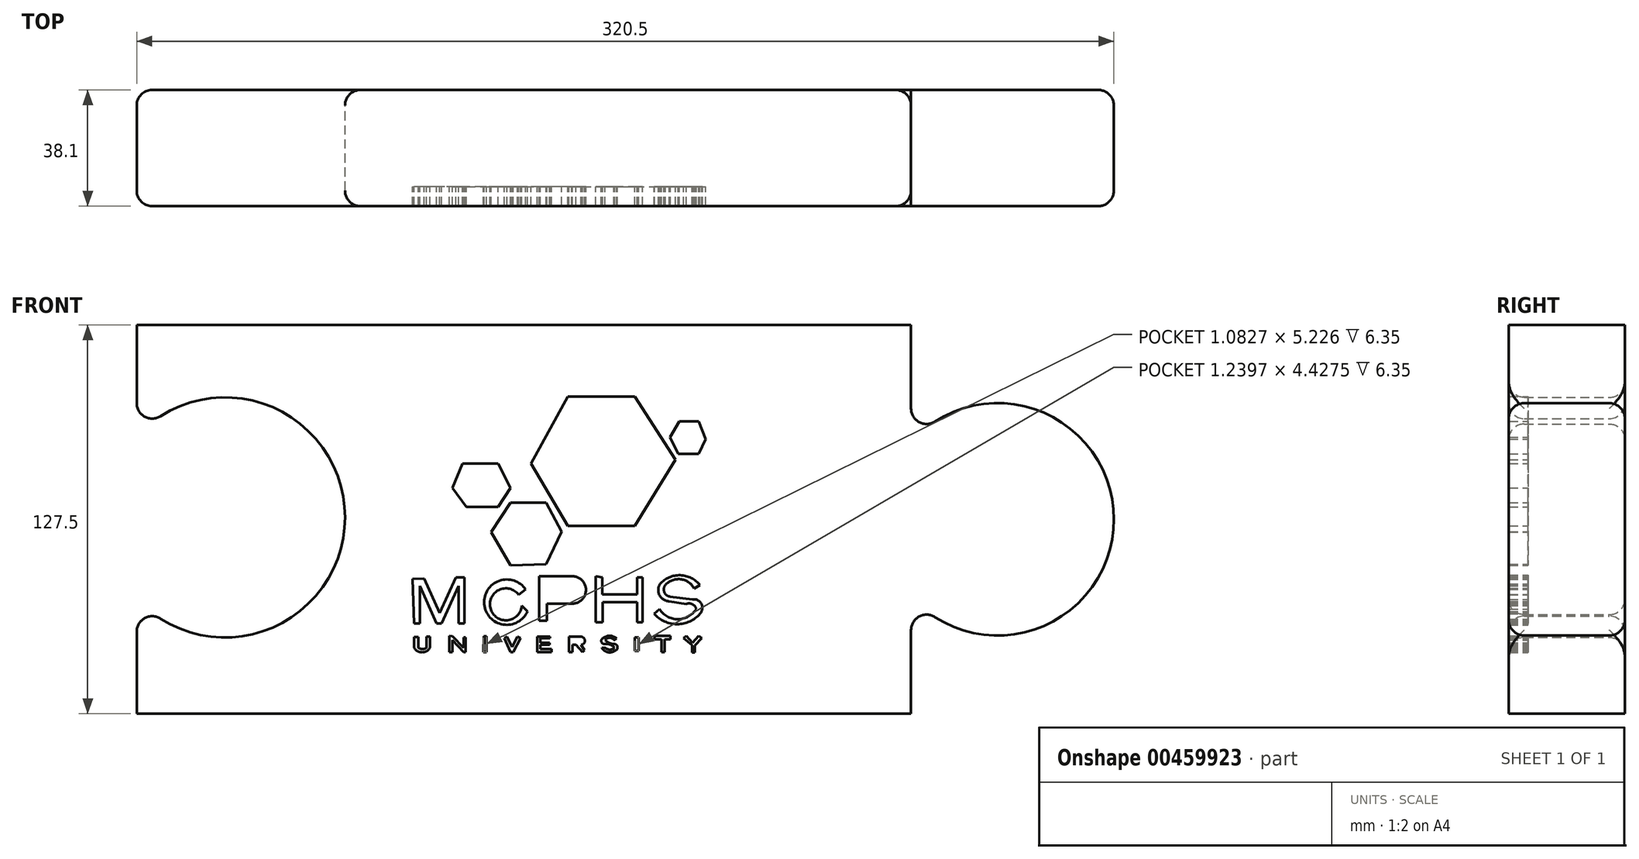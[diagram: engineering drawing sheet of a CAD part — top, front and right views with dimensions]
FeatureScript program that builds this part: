
annotation { "Feature Type Name" : "Feature", "Feature Type Description" : "" }
export const myFeature = defineFeature(function(context is Context, id is Id, definition is map)
    precondition{}
    {
        {
            var Q0;
            Q0=qCreatedBy(makeId("Front.planeOp"),FACE);
            var sketch = newSketch(context, id + "F0", { "sketchPlane" : qUnion([Q0])});
            skLineSegment(sketch, "E0", {"start": v(-152.36, 71.31) * mm, "end": v(101.64, 71.31) * mm, "construction": true});
            skLineSegment(sketch, "E1", {"start": v(-152.36, -56.2) * mm, "end": v(101.64, -56.2) * mm, "construction": true});
            skArc(sketch, "E2", {"start": v(101.64, -17.84) * mm, "mid": v(168.14, 7.56) * mm, "end": v(101.64, 32.96) * mm, "construction": true});
            skLineSegment(sketch, "E3", {"start": v(-152.36, -56.2) * mm, "end": v(-152.36, -18.47) * mm});
            skLineSegment(sketch, "E4", {"start": v(-152.36, -56.2) * mm, "end": v(101.64, -56.2) * mm});
            skLineSegment(sketch, "E5", {"start": v(101.64, -17.84) * mm, "end": v(101.64, -56.2) * mm});
            skLineSegment(sketch, "E6", {"start": v(101.64, 32.96) * mm, "end": v(101.64, 71.31) * mm});
            skLineSegment(sketch, "E7", {"start": v(-152.36, 71.31) * mm, "end": v(101.64, 71.31) * mm});
            skLineSegment(sketch, "E8", {"start": v(-152.36, 71.31) * mm, "end": v(-152.36, 34.87) * mm});
            skArc(sketch, "E9", {"start": v(-152.36, -18.47) * mm, "mid": v(-84.03, 8.2) * mm, "end": v(-152.36, 34.87) * mm});
            skArc(sketch, "E10", {"start": v(101.64, -17.84) * mm, "mid": v(168.14, 7.56) * mm, "end": v(101.64, 32.96) * mm});
            skLineSegment(sketch, "E11", {"start": v(-23.03, 25.82) * mm, "end": v(-10.96, 5.44) * mm});
            skLineSegment(sketch, "E12", {"start": v(-10.96, 5.44) * mm, "end": v(11.08, 5.44) * mm});
            skLineSegment(sketch, "E13", {"start": v(11.08, 5.44) * mm, "end": v(24.4, 27.07) * mm});
            skLineSegment(sketch, "E14", {"start": v(24.4, 27.07) * mm, "end": v(11.08, 47.87) * mm});
            skLineSegment(sketch, "E15", {"start": v(11.08, 47.87) * mm, "end": v(-10.96, 47.87) * mm});
            skLineSegment(sketch, "E16", {"start": v(-10.96, 47.87) * mm, "end": v(-23.03, 25.82) * mm});
            skLineSegment(sketch, "E17", {"start": v(-45.49, 25.82) * mm, "end": v(-33.84, 25.82) * mm});
            skLineSegment(sketch, "E18", {"start": v(-33.84, 25.82) * mm, "end": v(-29.68, 17.92) * mm});
            skLineSegment(sketch, "E19", {"start": v(-29.68, 17.92) * mm, "end": v(-33.84, 11.68) * mm});
            skLineSegment(sketch, "E20", {"start": v(-33.84, 11.68) * mm, "end": v(-44.24, 11.68) * mm});
            skLineSegment(sketch, "E21", {"start": v(-44.24, 11.68) * mm, "end": v(-48.82, 17.92) * mm});
            skLineSegment(sketch, "E22", {"start": v(-48.82, 17.92) * mm, "end": v(-45.49, 25.82) * mm});
            skLineSegment(sketch, "E23", {"start": v(-29.68, -7.55) * mm, "end": v(-36.12, 3.33) * mm});
            skLineSegment(sketch, "E24", {"start": v(-36.12, 3.33) * mm, "end": v(-29.68, 13) * mm});
            skLineSegment(sketch, "E25", {"start": v(-29.68, 13) * mm, "end": v(-18, 13) * mm});
            skLineSegment(sketch, "E26", {"start": v(-18, 13) * mm, "end": v(-12.99, 3.54) * mm});
            skLineSegment(sketch, "E27", {"start": v(-12.99, 3.54) * mm, "end": v(-18, -7.13) * mm});
            skLineSegment(sketch, "E28", {"start": v(-18, -7.13) * mm, "end": v(-29.68, -7.55) * mm});
            skLineSegment(sketch, "E29", {"start": v(22.57, 34.5) * mm, "end": v(25.3, 29.06) * mm});
            skLineSegment(sketch, "E30", {"start": v(25.3, 29.06) * mm, "end": v(31.99, 29.06) * mm});
            skLineSegment(sketch, "E31", {"start": v(31.99, 29.06) * mm, "end": v(34.29, 33.87) * mm});
            skLineSegment(sketch, "E32", {"start": v(34.29, 33.87) * mm, "end": v(31.99, 39.76) * mm});
            skLineSegment(sketch, "E33", {"start": v(31.99, 39.76) * mm, "end": v(25.66, 39.76) * mm});
            skLineSegment(sketch, "E34", {"start": v(25.66, 39.76) * mm, "end": v(22.57, 34.5) * mm});
            skLineSegment(sketch, "E35", {"start": v(-61.37, -26.57) * mm, "end": v(-59.5, -26.57) * mm});
            skLineSegment(sketch, "E36", {"start": v(-59.5, -26.57) * mm, "end": v(-59.5, -14.23) * mm});
            skLineSegment(sketch, "E37", {"start": v(-59.5, -14.23) * mm, "end": v(-54.05, -26.57) * mm});
            skLineSegment(sketch, "E38", {"start": v(-54.05, -26.57) * mm, "end": v(-52.38, -26.57) * mm});
            skLineSegment(sketch, "E39", {"start": v(-52.38, -26.57) * mm, "end": v(-46.73, -14.23) * mm});
            skLineSegment(sketch, "E40", {"start": v(-46.73, -14.23) * mm, "end": v(-46.73, -26.57) * mm});
            skLineSegment(sketch, "E41", {"start": v(-46.73, -26.57) * mm, "end": v(-44.85, -26.57) * mm});
            skLineSegment(sketch, "E42", {"start": v(-44.85, -26.57) * mm, "end": v(-44.85, -11.5) * mm});
            skLineSegment(sketch, "E43", {"start": v(-61.37, -26.57) * mm, "end": v(-61.9, -11.94) * mm});
            skLineSegment(sketch, "E44", {"start": v(-61.9, -11.94) * mm, "end": v(-58.03, -11.8) * mm});
            skLineSegment(sketch, "E45", {"start": v(-58.03, -11.8) * mm, "end": v(-53, -23.22) * mm});
            skLineSegment(sketch, "E46", {"start": v(-53, -23.22) * mm, "end": v(-47.64, -11.5) * mm});
            skLineSegment(sketch, "E47", {"start": v(-47.64, -11.5) * mm, "end": v(-44.85, -11.5) * mm});
            skArc(sketch, "E48", {"start": v(-24.77, -15.48) * mm, "mid": v(-38.37, -20.26) * mm, "end": v(-24.14, -22.6) * mm});
            skLineSegment(sketch, "E49", {"start": v(-24.14, -22.6) * mm, "end": v(-26.02, -20.7) * mm});
            skLineSegment(sketch, "E50", {"start": v(-24.77, -15.48) * mm, "end": v(-27.07, -17.15) * mm});
            skArc(sketch, "E51", {"start": v(-27.07, -17.15) * mm, "mid": v(-36.27, -21.8) * mm, "end": v(-26.02, -20.7) * mm});
            skLineSegment(sketch, "E52", {"start": v(-17.86, -25.73) * mm, "end": v(-20.37, -25.73) * mm});
            skLineSegment(sketch, "E53", {"start": v(-20.37, -25.73) * mm, "end": v(-20.37, -11.09) * mm});
            skLineSegment(sketch, "E54", {"start": v(-20.37, -11.09) * mm, "end": v(-9.5, -11.09) * mm});
            skLineSegment(sketch, "E55", {"start": v(-17.86, -25.73) * mm, "end": v(-17.86, -20.08) * mm});
            skLineSegment(sketch, "E56", {"start": v(-17.86, -20.08) * mm, "end": v(-9.7, -20.08) * mm});
            skLineSegment(sketch, "E57", {"start": v(-17.86, -17.78) * mm, "end": v(-18.03, -13.17) * mm});
            skLineSegment(sketch, "E58", {"start": v(-18.03, -13.17) * mm, "end": v(-10.33, -13.17) * mm});
            skLineSegment(sketch, "E59", {"start": v(-17.86, -17.78) * mm, "end": v(-9.7, -17.49) * mm});
            skArc(sketch, "E60", {"start": v(-9.7, -17.49) * mm, "mid": v(-7.61, -14.98) * mm, "end": v(-10.33, -13.17) * mm});
            skArc(sketch, "E61", {"start": v(-9.7, -20.08) * mm, "mid": v(-5, -15.69) * mm, "end": v(-9.5, -11.09) * mm});
            skLineSegment(sketch, "E62", {"start": v(0.34, -17.1) * mm, "end": v(0.34, -11.46) * mm});
            skLineSegment(sketch, "E63", {"start": v(0.34, -17.1) * mm, "end": v(11.84, -17.1) * mm});
            skLineSegment(sketch, "E64", {"start": v(11.84, -17.57) * mm, "end": v(11.84, -11.46) * mm});
            skLineSegment(sketch, "E65", {"start": v(11.84, -11.46) * mm, "end": v(13.52, -11.46) * mm});
            skLineSegment(sketch, "E66", {"start": v(13.52, -11.46) * mm, "end": v(13.52, -26.15) * mm});
            skLineSegment(sketch, "E67", {"start": v(13.52, -26.15) * mm, "end": v(11.84, -26.15) * mm});
            skLineSegment(sketch, "E68", {"start": v(11.84, -26.15) * mm, "end": v(11.84, -19.57) * mm});
            skLineSegment(sketch, "E69", {"start": v(11.84, -19.57) * mm, "end": v(0.44, -19.57) * mm});
            skLineSegment(sketch, "E70", {"start": v(0.44, -19.57) * mm, "end": v(0.44, -26.15) * mm});
            skLineSegment(sketch, "E71", {"start": v(0.44, -26.15) * mm, "end": v(-1.84, -26.15) * mm});
            skLineSegment(sketch, "E72", {"start": v(-1.84, -26.15) * mm, "end": v(-1.84, -11.11) * mm});
            skLineSegment(sketch, "E73", {"start": v(-1.84, -11.11) * mm, "end": v(0.34, -11.46) * mm});
            skArc(sketch, "E74", {"start": v(32.42, -14.05) * mm, "mid": v(25.94, -10.78) * mm, "end": v(19.29, -13.67) * mm});
            skLineSegment(sketch, "E75", {"start": v(32.42, -14.05) * mm, "end": v(30.44, -15.1) * mm});
            skLineSegment(sketch, "E76", {"start": v(19.1, -21.86) * mm, "end": v(17.38, -23.38) * mm});
            skPoint(sketch, "E77.endSnap0", {"position": v(13.52, -18.8) * mm});
            skArc(sketch, "E78", {"start": v(19.1, -21.86) * mm, "mid": v(25.14, -25.2) * mm, "end": v(31.18, -21.86) * mm});
            skArc(sketch, "E79", {"start": v(31.18, -21.86) * mm, "mid": v(29.92, -20.3) * mm, "end": v(27.92, -20.18) * mm});
            skArc(sketch, "E80", {"start": v(19.29, -13.67) * mm, "mid": v(19.16, -17.38) * mm, "end": v(22.33, -19.32) * mm});
            skLineSegment(sketch, "E81", {"start": v(22.33, -19.32) * mm, "end": v(27.92, -20.18) * mm});
            skArc(sketch, "E82", {"start": v(30.44, -15.1) * mm, "mid": v(26, -12.08) * mm, "end": v(21.01, -14.05) * mm});
            skArc(sketch, "E83", {"start": v(21.01, -14.05) * mm, "mid": v(20.72, -16.36) * mm, "end": v(22.57, -17.78) * mm});
            skArc(sketch, "E84", {"start": v(17.38, -23.38) * mm, "mid": v(24.9, -26.81) * mm, "end": v(32.42, -23.38) * mm});
            skArc(sketch, "E85", {"start": v(32.42, -23.38) * mm, "mid": v(32.86, -20.13) * mm, "end": v(29.92, -18.7) * mm});
            skPoint(sketch, "E85.endSnap0", {"position": v(29.92, -20.3) * mm});
            skLineSegment(sketch, "E86", {"start": v(22.57, -17.78) * mm, "end": v(29.92, -18.7) * mm});
            skLineSegment(sketch, "E87", {"start": v(-61.32, -31.06) * mm, "end": v(-61.32, -34.58) * mm});
            skLineSegment(sketch, "E88", {"start": v(-56.2, -30.93) * mm, "end": v(-56.2, -34.58) * mm});
            skLineSegment(sketch, "E89", {"start": v(-56.2, -30.93) * mm, "end": v(-57.3, -30.93) * mm});
            skLineSegment(sketch, "E90", {"start": v(-57.3, -30.93) * mm, "end": v(-57.3, -34.58) * mm});
            skLineSegment(sketch, "E91", {"start": v(-61.32, -31.06) * mm, "end": v(-59.93, -31.06) * mm});
            skLineSegment(sketch, "E92", {"start": v(-59.93, -31.06) * mm, "end": v(-59.93, -34.58) * mm});
            skArc(sketch, "E93", {"start": v(-61.32, -34.58) * mm, "mid": v(-58.76, -36.06) * mm, "end": v(-56.2, -34.58) * mm});
            skArc(sketch, "E94", {"start": v(-59.93, -34.58) * mm, "mid": v(-58.62, -34.98) * mm, "end": v(-57.3, -34.58) * mm});
            skLineSegment(sketch, "E95", {"start": v(-49.86, -35.96) * mm, "end": v(-48.85, -35.96) * mm});
            skLineSegment(sketch, "E96", {"start": v(-48.85, -35.96) * mm, "end": v(-48.85, -32.07) * mm});
            skLineSegment(sketch, "E97", {"start": v(-48.85, -32.07) * mm, "end": v(-45.16, -35.96) * mm});
            skLineSegment(sketch, "E98", {"start": v(-45.16, -35.96) * mm, "end": v(-44.48, -35.96) * mm});
            skLineSegment(sketch, "E99", {"start": v(-44.48, -35.96) * mm, "end": v(-44.48, -31.18) * mm});
            skLineSegment(sketch, "E100", {"start": v(-44.48, -31.18) * mm, "end": v(-45.16, -31.18) * mm});
            skLineSegment(sketch, "E101", {"start": v(-45.16, -31.18) * mm, "end": v(-45.16, -34.62) * mm});
            skLineSegment(sketch, "E102", {"start": v(-45.16, -34.62) * mm, "end": v(-48.85, -30.73) * mm});
            skLineSegment(sketch, "E103", {"start": v(-49.86, -35.96) * mm, "end": v(-49.86, -30.61) * mm});
            skLineSegment(sketch, "E104", {"start": v(-49.86, -30.61) * mm, "end": v(-48.85, -30.73) * mm});
            skLineSegment(sketch, "E105", {"start": v(-38.66, -35.96) * mm, "end": v(-37.58, -35.96) * mm});
            skLineSegment(sketch, "E106", {"start": v(-37.58, -35.96) * mm, "end": v(-37.58, -30.73) * mm});
            skLineSegment(sketch, "E107", {"start": v(-37.58, -30.73) * mm, "end": v(-38.57, -30.73) * mm});
            skLineSegment(sketch, "E108", {"start": v(-38.57, -30.73) * mm, "end": v(-38.66, -35.96) * mm});
            skLineSegment(sketch, "E109", {"start": v(-31.77, -31.4) * mm, "end": v(-29.76, -35.96) * mm});
            skLineSegment(sketch, "E110", {"start": v(-29.76, -35.96) * mm, "end": v(-28.83, -35.96) * mm});
            skLineSegment(sketch, "E111", {"start": v(-28.83, -35.96) * mm, "end": v(-26.46, -31.42) * mm});
            skLineSegment(sketch, "E112", {"start": v(-26.46, -31.42) * mm, "end": v(-27.4, -30.94) * mm});
            skLineSegment(sketch, "E113", {"start": v(-27.4, -30.94) * mm, "end": v(-29.2, -34.38) * mm});
            skLineSegment(sketch, "E114", {"start": v(-29.2, -34.38) * mm, "end": v(-30.9, -30.94) * mm});
            skLineSegment(sketch, "E115", {"start": v(-30.9, -30.94) * mm, "end": v(-31.77, -31.4) * mm});
            skLineSegment(sketch, "E116", {"start": v(-20.96, -30.94) * mm, "end": v(-20.96, -35.96) * mm});
            skLineSegment(sketch, "E117", {"start": v(-20.96, -35.96) * mm, "end": v(-16.22, -35.96) * mm});
            skLineSegment(sketch, "E118", {"start": v(-16.22, -35.96) * mm, "end": v(-16.22, -35.01) * mm});
            skLineSegment(sketch, "E119", {"start": v(-16.22, -35.01) * mm, "end": v(-19.92, -35.01) * mm});
            skLineSegment(sketch, "E120", {"start": v(-19.92, -35.01) * mm, "end": v(-19.92, -33.61) * mm});
            skLineSegment(sketch, "E121", {"start": v(-19.92, -33.61) * mm, "end": v(-16.97, -33.61) * mm});
            skLineSegment(sketch, "E122", {"start": v(-16.97, -33.61) * mm, "end": v(-16.97, -32.9) * mm});
            skLineSegment(sketch, "E123", {"start": v(-16.97, -32.9) * mm, "end": v(-19.92, -32.9) * mm});
            skLineSegment(sketch, "E124", {"start": v(-19.92, -32.9) * mm, "end": v(-19.92, -31.4) * mm});
            skLineSegment(sketch, "E125", {"start": v(-19.92, -31.4) * mm, "end": v(-16.75, -31.42) * mm});
            skLineSegment(sketch, "E126", {"start": v(-16.75, -31.42) * mm, "end": v(-16.75, -30.94) * mm});
            skLineSegment(sketch, "E127", {"start": v(-16.75, -30.94) * mm, "end": v(-20.96, -30.94) * mm});
            skLineSegment(sketch, "E128", {"start": v(-10.55, -35.96) * mm, "end": v(-9.45, -35.96) * mm});
            skLineSegment(sketch, "E129", {"start": v(-10.55, -35.96) * mm, "end": v(-10.55, -30.94) * mm});
            skLineSegment(sketch, "E130", {"start": v(-10.55, -30.94) * mm, "end": v(-6.69, -30.94) * mm});
            skLineSegment(sketch, "E131", {"start": v(-9.45, -35.96) * mm, "end": v(-9.45, -33.61) * mm});
            skLineSegment(sketch, "E132", {"start": v(-9.45, -33.61) * mm, "end": v(-8.23, -33.61) * mm});
            skLineSegment(sketch, "E133", {"start": v(-8.23, -33.61) * mm, "end": v(-6.16, -35.96) * mm});
            skLineSegment(sketch, "E134", {"start": v(-6.16, -35.96) * mm, "end": v(-5.43, -35.31) * mm});
            skLineSegment(sketch, "E135", {"start": v(-5.43, -35.31) * mm, "end": v(-6.69, -33.61) * mm});
            skLineSegment(sketch, "E136", {"start": v(-9.45, -31.42) * mm, "end": v(-9.45, -32.9) * mm});
            skLineSegment(sketch, "E137", {"start": v(-9.45, -31.42) * mm, "end": v(-7.2, -31.42) * mm});
            skLineSegment(sketch, "E138", {"start": v(-9.45, -32.9) * mm, "end": v(-7.28, -32.9) * mm});
            skArc(sketch, "E139", {"start": v(-7.28, -32.9) * mm, "mid": v(-6.54, -32.2) * mm, "end": v(-7.2, -31.42) * mm});
            skArc(sketch, "E140", {"start": v(-6.69, -33.61) * mm, "mid": v(-5.35, -32.27) * mm, "end": v(-6.69, -30.94) * mm});
            skLineSegment(sketch, "E141", {"start": v(11, -31.22) * mm, "end": v(11, -35.64) * mm});
            skLineSegment(sketch, "E142", {"start": v(11, -35.64) * mm, "end": v(12.24, -35.64) * mm});
            skLineSegment(sketch, "E143", {"start": v(12.24, -35.64) * mm, "end": v(12.24, -31.22) * mm});
            skLineSegment(sketch, "E144", {"start": v(12.24, -31.22) * mm, "end": v(11, -31.22) * mm});
            skLineSegment(sketch, "E145", {"start": v(0.21, -34.57) * mm, "end": v(1.3, -34.57) * mm});
            skLineSegment(sketch, "E146", {"start": v(4.23, -32.05) * mm, "end": v(5.05, -31.5) * mm});
            skArc(sketch, "E147", {"start": v(5.05, -31.5) * mm, "mid": v(2.77, -30.65) * mm, "end": v(0.49, -31.5) * mm});
            skArc(sketch, "E148", {"start": v(1.3, -34.57) * mm, "mid": v(2.84, -35.2) * mm, "end": v(4.37, -34.57) * mm});
            skArc(sketch, "E149", {"start": v(4.23, -32.05) * mm, "mid": v(2.77, -31.29) * mm, "end": v(1.3, -32.05) * mm});
            skArc(sketch, "E150", {"start": v(0.49, -31.5) * mm, "mid": v(0.1, -32.76) * mm, "end": v(1.3, -33.3) * mm});
            skArc(sketch, "E151", {"start": v(4.37, -34.57) * mm, "mid": v(2.99, -33.57) * mm, "end": v(1.3, -33.3) * mm});
            skArc(sketch, "E152", {"start": v(1.3, -32.05) * mm, "mid": v(2.69, -33.04) * mm, "end": v(4.37, -33.3) * mm});
            skArc(sketch, "E153", {"start": v(4.37, -35.6) * mm, "mid": v(5.37, -34.45) * mm, "end": v(4.37, -33.3) * mm});
            skArc(sketch, "E154", {"start": v(0.21, -34.57) * mm, "mid": v(2.06, -36) * mm, "end": v(4.37, -35.6) * mm});
            skLineSegment(sketch, "E155", {"start": v(19.77, -31.74) * mm, "end": v(19.77, -36.05) * mm});
            skLineSegment(sketch, "E156", {"start": v(19.77, -36.05) * mm, "end": v(20.82, -36.05) * mm});
            skLineSegment(sketch, "E157", {"start": v(20.82, -36.05) * mm, "end": v(20.82, -31.74) * mm});
            skLineSegment(sketch, "E158", {"start": v(20.82, -31.74) * mm, "end": v(22.76, -31.74) * mm});
            skLineSegment(sketch, "E159", {"start": v(22.76, -31.74) * mm, "end": v(22.76, -30.7) * mm});
            skLineSegment(sketch, "E160", {"start": v(22.76, -30.7) * mm, "end": v(17.55, -30.7) * mm});
            skLineSegment(sketch, "E161", {"start": v(17.55, -30.7) * mm, "end": v(17.55, -31.74) * mm});
            skLineSegment(sketch, "E162", {"start": v(27.07, -31.46) * mm, "end": v(27.9, -30.7) * mm});
            skLineSegment(sketch, "E163", {"start": v(27.07, -31.46) * mm, "end": v(29.78, -33.76) * mm});
            skLineSegment(sketch, "E164", {"start": v(29.78, -33.76) * mm, "end": v(29.78, -36.12) * mm});
            skLineSegment(sketch, "E165", {"start": v(29.78, -36.12) * mm, "end": v(30.75, -36.12) * mm});
            skLineSegment(sketch, "E166", {"start": v(30.75, -36.12) * mm, "end": v(30.75, -33.9) * mm});
            skLineSegment(sketch, "E167", {"start": v(30.75, -33.9) * mm, "end": v(33.04, -31.46) * mm});
            skLineSegment(sketch, "E168", {"start": v(17.55, -31.74) * mm, "end": v(19.77, -31.74) * mm});
            skLineSegment(sketch, "E169", {"start": v(27.9, -30.7) * mm, "end": v(29.98, -32.96) * mm});
            skLineSegment(sketch, "E170", {"start": v(29.98, -32.96) * mm, "end": v(31.95, -30.7) * mm});
            skLineSegment(sketch, "E171", {"start": v(31.95, -30.7) * mm, "end": v(33.04, -31.46) * mm});
            skSolve(sketch);
        }
        {
            var Q0;
            Q0 = qSketchRegion(id + "F0", true);
            var Q1;
            Q1 = qConstructionFilter(qBodyType(qCreatedBy(id + "F0" ,EDGE), BodyType.WIRE), ConstructionObject.NO);
            extrude(context, id + "F1", {"entities" : qUnion([Q0]), "surfaceEntities" : qUnion([Q1]), "depth" : 38.1 * mm});
        }
        {
            var Q0;
            Q0=makeQuery(id+"F1.opExtrude","CAP_FACE",FACE,{"disambiguationData":[OSD([sQuery(id+"F0.wireOp",EDGE,"E3"),sQuery(id+"F0.wireOp",EDGE,"E4"),sQuery(id+"F0.wireOp",EDGE,"E5"),sQuery(id+"F0.wireOp",EDGE,"E6"),sQuery(id+"F0.wireOp",EDGE,"E7"),sQuery(id+"F0.wireOp",EDGE,"E8"),sQuery(id+"F0.wireOp",EDGE,"E9"),sQuery(id+"F0.wireOp",EDGE,"E10")])],"isStart":true});
            var sketch = newSketch(context, id + "F2", { "sketchPlane" : qUnion([Q0])});
            skLineSegment(sketch, "E172.bottom", {"start": v(-40.13, 53.08) * mm, "end": v(79.46, 53.08) * mm});
            skLineSegment(sketch, "E172.top", {"start": v(-40.13, -47.5) * mm, "end": v(79.46, -47.5) * mm});
            skLineSegment(sketch, "E172.left", {"start": v(-40.13, 53.08) * mm, "end": v(-40.13, -47.5) * mm});
            skLineSegment(sketch, "E172.right", {"start": v(79.46, 53.08) * mm, "end": v(79.46, -47.5) * mm});
            skSolve(sketch);
        }
        {
            var Q0;
            Q0 = qSketchRegion(id + "F2", true);
            extrude(context, id + "F3", {"entities" : qUnion([Q0]), "operationType" : NewBodyOperationType.ADD, "oppositeDirection" : true, "depth" : 31.75 * mm});
        }
        {
            var Q0;
            Q0=makeQuery(id+"F1.opExtrude","SWEPT_EDGE",EDGE,{"disambiguationData":[OSD([sQuery(id+"F0.wireOp",EDGE,"E8"),sQuery(id+"F0.wireOp",EDGE,"E9")])]});
            var Q1;
            Q1=makeQuery(id+"F1.opExtrude","CAP_EDGE",EDGE,{"disambiguationData":[OSD([sQuery(id+"F0.wireOp",EDGE,"E9")])],"isStart":false});
            var Q2;
            Q2=makeQuery(id+"F1.opExtrude","CAP_EDGE",EDGE,{"disambiguationData":[OSD([sQuery(id+"F0.wireOp",EDGE,"E9")])],"isStart":true});
            var Q3;
            Q3=makeQuery(id+"F1.opExtrude","SWEPT_EDGE",EDGE,{"disambiguationData":[OSD([sQuery(id+"F0.wireOp",EDGE,"E3"),sQuery(id+"F0.wireOp",EDGE,"E9")])]});
            var Q4;
            Q4=makeQuery(id+"F1.opExtrude","CAP_EDGE",EDGE,{"disambiguationData":[OSD([sQuery(id+"F0.wireOp",EDGE,"E8")])],"isStart":false});
            var Q5;
            Q5=makeQuery(id+"F1.opExtrude","CAP_EDGE",EDGE,{"disambiguationData":[OSD([sQuery(id+"F0.wireOp",EDGE,"E3")])],"isStart":false});
            var Q6;
            Q6=makeQuery(id+"F1.opExtrude","CAP_EDGE",EDGE,{"disambiguationData":[OSD([sQuery(id+"F0.wireOp",EDGE,"E3")])],"isStart":true});
            var Q7;
            Q7=makeQuery(id+"F1.opExtrude","CAP_EDGE",EDGE,{"disambiguationData":[OSD([sQuery(id+"F0.wireOp",EDGE,"E8")])],"isStart":true});
            fillet(context, id + "F4", {"entities" : qUnion([Q0, Q1, Q2, Q3, Q4, Q5, Q6, Q7]), "radius" : 5.08 * mm, "tangentPropagation" : true, "allowEdgeOverflow" : false});
        }
        {
            var Q0;
            Q0=makeQuery(id+"F1.opExtrude","SWEPT_EDGE",EDGE,{"disambiguationData":[OSD([sQuery(id+"F0.wireOp",EDGE,"E6"),sQuery(id+"F0.wireOp",EDGE,"E10")])]});
            var Q1;
            Q1=makeQuery(id+"F1.opExtrude","SWEPT_EDGE",EDGE,{"disambiguationData":[OSD([sQuery(id+"F0.wireOp",EDGE,"E5"),sQuery(id+"F0.wireOp",EDGE,"E10")])]});
            var Q2;
            Q2=makeQuery(id+"F1.opExtrude","CAP_EDGE",EDGE,{"disambiguationData":[OSD([sQuery(id+"F0.wireOp",EDGE,"E10")])],"isStart":false});
            var Q3;
            Q3=makeQuery(id+"F1.opExtrude","CAP_EDGE",EDGE,{"disambiguationData":[OSD([sQuery(id+"F0.wireOp",EDGE,"E10")])],"isStart":true});
            fillet(context, id + "F5", {"entities" : qUnion([Q0, Q1, Q2, Q3]), "radius" : 5.08 * mm, "tangentPropagation" : true, "allowEdgeOverflow" : false});
        }
    });
